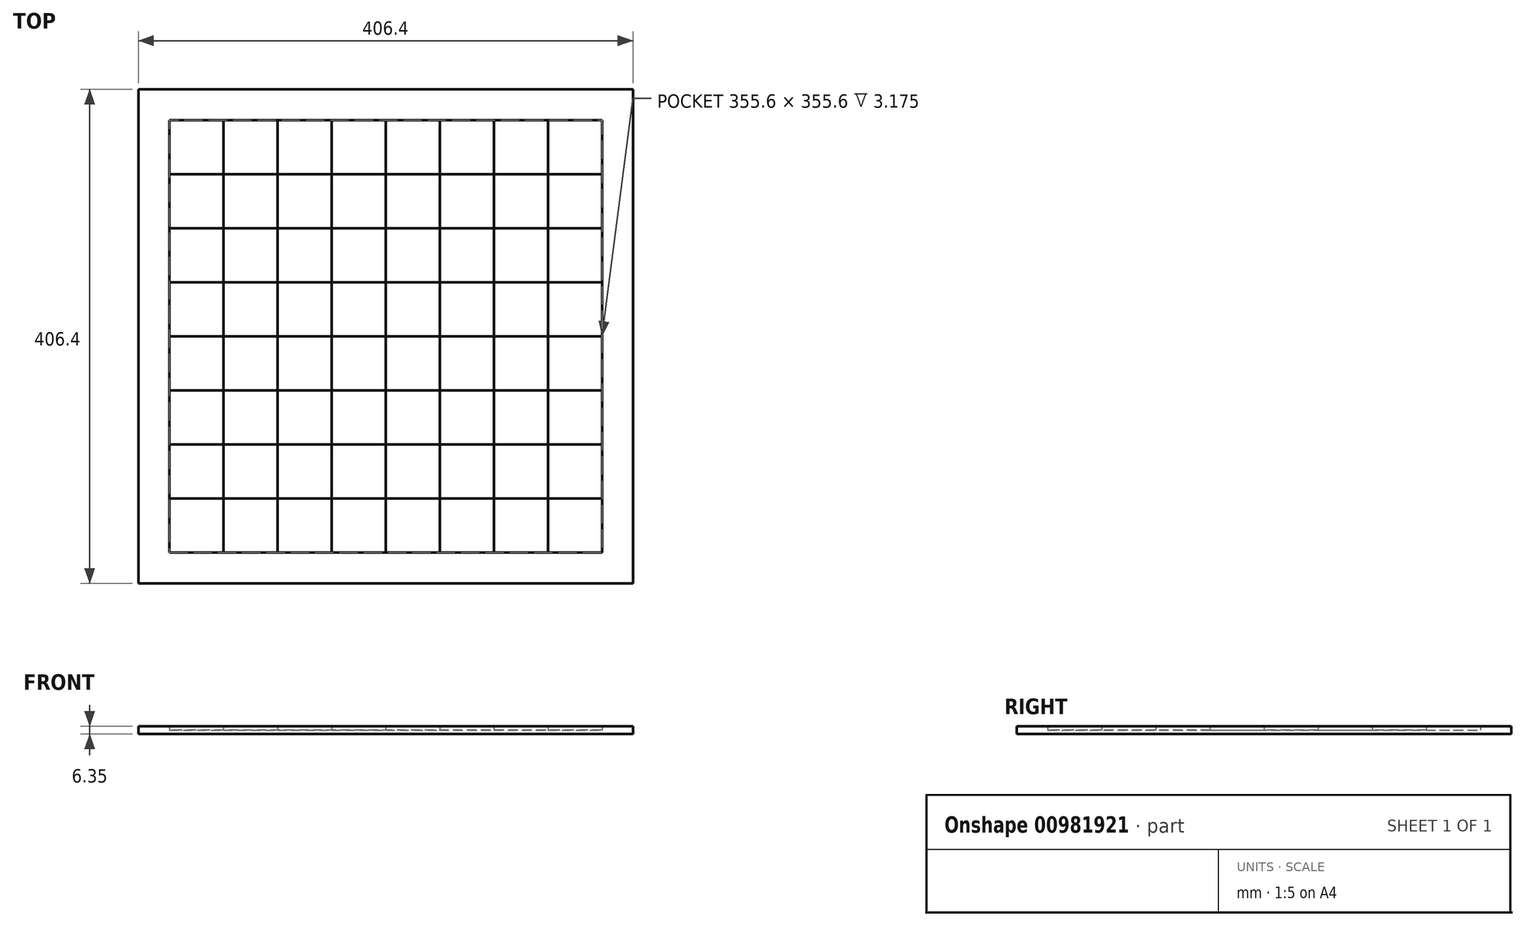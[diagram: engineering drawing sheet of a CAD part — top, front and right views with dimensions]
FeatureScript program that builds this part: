
annotation { "Feature Type Name" : "Feature", "Feature Type Description" : "" }
export const myFeature = defineFeature(function(context is Context, id is Id, definition is map)
    precondition{}
    {
        {
            var Q0;
            Q0=qCreatedBy(makeId("Top.planeOp"),FACE);
            var sketch = newSketch(context, id + "F0", { "sketchPlane" : qUnion([Q0])});
            skLineSegment(sketch, "E0.bottom", {"start": v(203.2, 203.2) * mm, "end": v(-203.2, 203.2) * mm});
            skLineSegment(sketch, "E0.top", {"start": v(203.2, -203.2) * mm, "end": v(-203.2, -203.2) * mm});
            skLineSegment(sketch, "E0.left", {"start": v(203.2, 203.2) * mm, "end": v(203.2, -203.2) * mm});
            skLineSegment(sketch, "E0.right", {"start": v(-203.2, 203.2) * mm, "end": v(-203.2, -203.2) * mm});
            skPoint(sketch, "E0.middle", {"position": v(0, 0) * mm});
            skSolve(sketch);
        }
        {
            var Q0;
            Q0 = qSketchRegion(id + "F0", true);
            extrude(context, id + "F1", {"entities" : qUnion([Q0]), "depth" : 3.17 * mm, "offsetDistance" : 25.4 * mm});
        }
        {
            var Q0;
            Q0=makeQuery(id+"F1.opExtrude","CAP_FACE",FACE,{"disambiguationData":[OSD([sQuery(id+"F0.wireOp",EDGE,"E0.bottom"),sQuery(id+"F0.wireOp",EDGE,"E0.top"),sQuery(id+"F0.wireOp",EDGE,"E0.left"),sQuery(id+"F0.wireOp",EDGE,"E0.right")])],"isStart":false});
            var sketch = newSketch(context, id + "F2", { "sketchPlane" : qUnion([Q0])});
            skLineSegment(sketch, "E1.bottom", {"start": v(203.2, -203.2) * mm, "end": v(-203.2, -203.2) * mm});
            skLineSegment(sketch, "E1.top", {"start": v(203.2, 203.2) * mm, "end": v(-203.2, 203.2) * mm});
            skLineSegment(sketch, "E1.left", {"start": v(203.2, -203.2) * mm, "end": v(203.2, 203.2) * mm});
            skLineSegment(sketch, "E1.right", {"start": v(-203.2, -203.2) * mm, "end": v(-203.2, 203.2) * mm});
            skPoint(sketch, "E1.middle", {"position": v(0, 0) * mm});
            skLineSegment(sketch, "E2.bottom", {"start": v(177.8, -177.8) * mm, "end": v(-177.8, -177.8) * mm});
            skLineSegment(sketch, "E2.top", {"start": v(177.8, 177.8) * mm, "end": v(-177.8, 177.8) * mm});
            skLineSegment(sketch, "E2.left", {"start": v(177.8, -177.8) * mm, "end": v(177.8, 177.8) * mm});
            skLineSegment(sketch, "E2.right", {"start": v(-177.8, -177.8) * mm, "end": v(-177.8, 177.8) * mm});
            skSolve(sketch);
        }
        {
            var Q0;
            Q0 = qSketchRegion(id + "F2", true);
            extrude(context, id + "F3", {"entities" : qUnion([Q0]), "operationType" : NewBodyOperationType.ADD, "depth" : 3.17 * mm, "offsetDistance" : 25.4 * mm});
        }
        {
            var Q0;
            Q0=makeQuery(id+"F1.opExtrude","CAP_FACE",FACE,{"disambiguationData":[OSD([sQuery(id+"F0.wireOp",EDGE,"E0.bottom"),sQuery(id+"F0.wireOp",EDGE,"E0.top"),sQuery(id+"F0.wireOp",EDGE,"E0.left"),sQuery(id+"F0.wireOp",EDGE,"E0.right")])],"isStart":false});
            var sketch = newSketch(context, id + "F4", { "sketchPlane" : qUnion([Q0])});
            skLineSegment(sketch, "E3.bottom", {"start": v(-177.8, 177.8) * mm, "end": v(-133.35, 177.8) * mm});
            skLineSegment(sketch, "E3.top", {"start": v(-177.8, 133.35) * mm, "end": v(-133.35, 133.35) * mm});
            skLineSegment(sketch, "E3.left", {"start": v(-177.8, 177.8) * mm, "end": v(-177.8, 133.35) * mm});
            skLineSegment(sketch, "E3.right", {"start": v(-133.35, 177.8) * mm, "end": v(-133.35, 133.35) * mm});
            skLineSegment(sketch, "E4.1.0.0", {"start": v(-44.45, 177.8) * mm, "end": v(-44.45, 133.35) * mm});
            skLineSegment(sketch, "E4.1.0.1", {"start": v(-88.9, 133.35) * mm, "end": v(-44.45, 133.35) * mm});
            skLineSegment(sketch, "E4.1.0.2", {"start": v(-88.9, 177.8) * mm, "end": v(-88.9, 133.35) * mm});
            skLineSegment(sketch, "E4.1.0.3", {"start": v(-88.9, 177.8) * mm, "end": v(-44.45, 177.8) * mm});
            skLineSegment(sketch, "E4.2.0.0", {"start": v(44.45, 177.8) * mm, "end": v(44.45, 133.35) * mm});
            skLineSegment(sketch, "E4.2.0.1", {"start": v(0, 133.35) * mm, "end": v(44.45, 133.35) * mm});
            skLineSegment(sketch, "E4.2.0.2", {"start": v(0, 177.8) * mm, "end": v(0, 133.35) * mm});
            skLineSegment(sketch, "E4.2.0.3", {"start": v(0, 177.8) * mm, "end": v(44.45, 177.8) * mm});
            skLineSegment(sketch, "E4.3.0.0", {"start": v(133.35, 177.8) * mm, "end": v(133.35, 133.35) * mm});
            skLineSegment(sketch, "E4.3.0.1", {"start": v(88.9, 133.35) * mm, "end": v(133.35, 133.35) * mm});
            skLineSegment(sketch, "E4.3.0.2", {"start": v(88.9, 177.8) * mm, "end": v(88.9, 133.35) * mm});
            skLineSegment(sketch, "E4.3.0.3", {"start": v(88.9, 177.8) * mm, "end": v(133.35, 177.8) * mm});
            skLineSegment(sketch, "E4.direction1", {"start": v(-177.8, 133.35) * mm, "end": v(-88.9, 133.35) * mm, "construction": true});
            skLineSegment(sketch, "E5.bottom", {"start": v(-133.35, 133.35) * mm, "end": v(-88.9, 133.35) * mm});
            skLineSegment(sketch, "E5.top", {"start": v(-133.35, 88.9) * mm, "end": v(-88.9, 88.9) * mm});
            skLineSegment(sketch, "E5.left", {"start": v(-133.35, 133.35) * mm, "end": v(-133.35, 88.9) * mm});
            skLineSegment(sketch, "E5.right", {"start": v(-88.9, 133.35) * mm, "end": v(-88.9, 88.9) * mm});
            skLineSegment(sketch, "E6.1.0.0", {"start": v(-44.45, 133.35) * mm, "end": v(-44.45, 88.9) * mm});
            skLineSegment(sketch, "E6.1.0.1", {"start": v(-44.45, 88.9) * mm, "end": v(0, 88.9) * mm});
            skLineSegment(sketch, "E6.1.0.2", {"start": v(0, 133.35) * mm, "end": v(0, 88.9) * mm});
            skLineSegment(sketch, "E6.1.0.3", {"start": v(-44.45, 133.35) * mm, "end": v(0, 133.35) * mm});
            skLineSegment(sketch, "E6.2.0.0", {"start": v(44.45, 133.35) * mm, "end": v(44.45, 88.9) * mm});
            skLineSegment(sketch, "E6.2.0.1", {"start": v(44.45, 88.9) * mm, "end": v(88.9, 88.9) * mm});
            skLineSegment(sketch, "E6.2.0.2", {"start": v(88.9, 133.35) * mm, "end": v(88.9, 88.9) * mm});
            skLineSegment(sketch, "E6.2.0.3", {"start": v(44.45, 133.35) * mm, "end": v(88.9, 133.35) * mm});
            skLineSegment(sketch, "E6.3.0.0", {"start": v(133.35, 133.35) * mm, "end": v(133.35, 88.9) * mm});
            skLineSegment(sketch, "E6.3.0.1", {"start": v(133.35, 88.9) * mm, "end": v(177.8, 88.9) * mm});
            skLineSegment(sketch, "E6.3.0.2", {"start": v(177.8, 133.35) * mm, "end": v(177.8, 88.9) * mm});
            skLineSegment(sketch, "E6.3.0.3", {"start": v(133.35, 133.35) * mm, "end": v(177.8, 133.35) * mm});
            skLineSegment(sketch, "E6.direction1", {"start": v(-133.35, 88.9) * mm, "end": v(-44.45, 88.9) * mm, "construction": true});
            skLineSegment(sketch, "E7.0.1.0", {"start": v(-44.45, 44.45) * mm, "end": v(-44.45, 0) * mm});
            skLineSegment(sketch, "E7.0.1.1", {"start": v(-133.35, 44.45) * mm, "end": v(-133.35, 0) * mm});
            skLineSegment(sketch, "E7.0.1.2", {"start": v(-88.9, 88.9) * mm, "end": v(-88.9, 44.45) * mm});
            skLineSegment(sketch, "E7.0.1.3", {"start": v(-44.45, 88.9) * mm, "end": v(-44.45, 44.45) * mm});
            skLineSegment(sketch, "E7.0.1.4", {"start": v(88.9, 88.9) * mm, "end": v(88.9, 44.45) * mm});
            skLineSegment(sketch, "E7.0.1.5", {"start": v(133.35, 0) * mm, "end": v(177.8, 0) * mm});
            skLineSegment(sketch, "E7.0.1.6", {"start": v(44.45, 88.9) * mm, "end": v(44.45, 44.45) * mm});
            skLineSegment(sketch, "E7.0.1.7", {"start": v(-88.9, 44.45) * mm, "end": v(-44.45, 44.45) * mm});
            skLineSegment(sketch, "E7.0.1.8", {"start": v(44.45, 0) * mm, "end": v(88.9, 0) * mm});
            skLineSegment(sketch, "E7.0.1.9", {"start": v(133.35, 44.45) * mm, "end": v(177.8, 44.45) * mm});
            skLineSegment(sketch, "E7.0.1.10", {"start": v(0, 44.45) * mm, "end": v(0, 0) * mm});
            skLineSegment(sketch, "E7.0.1.11", {"start": v(-88.9, 44.45) * mm, "end": v(-88.9, 0) * mm});
            skLineSegment(sketch, "E7.0.1.12", {"start": v(44.45, 44.45) * mm, "end": v(44.45, 0) * mm});
            skLineSegment(sketch, "E7.0.1.13", {"start": v(-44.45, 44.45) * mm, "end": v(0, 44.45) * mm});
            skLineSegment(sketch, "E7.0.1.14", {"start": v(-177.8, 88.9) * mm, "end": v(-133.35, 88.9) * mm});
            skLineSegment(sketch, "E7.0.1.15", {"start": v(0, 44.45) * mm, "end": v(44.45, 44.45) * mm});
            skLineSegment(sketch, "E7.0.1.16", {"start": v(177.8, 44.45) * mm, "end": v(177.8, 0) * mm});
            skLineSegment(sketch, "E7.0.1.17", {"start": v(88.9, 44.45) * mm, "end": v(88.9, 0) * mm});
            skLineSegment(sketch, "E7.0.1.18", {"start": v(133.35, 88.9) * mm, "end": v(133.35, 44.45) * mm});
            skLineSegment(sketch, "E7.0.1.19", {"start": v(88.9, 88.9) * mm, "end": v(133.35, 88.9) * mm});
            skLineSegment(sketch, "E7.0.1.20", {"start": v(-133.35, 0) * mm, "end": v(-88.9, 0) * mm});
            skLineSegment(sketch, "E7.0.1.21", {"start": v(-44.45, 0) * mm, "end": v(0, 0) * mm});
            skLineSegment(sketch, "E7.0.1.22", {"start": v(-177.8, 44.45) * mm, "end": v(-133.35, 44.45) * mm});
            skLineSegment(sketch, "E7.0.1.23", {"start": v(0, 88.9) * mm, "end": v(0, 44.45) * mm});
            skLineSegment(sketch, "E7.0.1.24", {"start": v(44.45, 44.45) * mm, "end": v(88.9, 44.45) * mm});
            skLineSegment(sketch, "E7.0.1.25", {"start": v(133.35, 44.45) * mm, "end": v(133.35, 0) * mm});
            skLineSegment(sketch, "E7.0.1.26", {"start": v(88.9, 44.45) * mm, "end": v(133.35, 44.45) * mm});
            skLineSegment(sketch, "E7.0.1.27", {"start": v(-88.9, 88.9) * mm, "end": v(-44.45, 88.9) * mm});
            skLineSegment(sketch, "E7.0.1.28", {"start": v(-177.8, 88.9) * mm, "end": v(-177.8, 44.45) * mm});
            skLineSegment(sketch, "E7.0.1.29", {"start": v(-133.35, 88.9) * mm, "end": v(-133.35, 44.45) * mm});
            skLineSegment(sketch, "E7.0.1.30", {"start": v(-133.35, 44.45) * mm, "end": v(-88.9, 44.45) * mm});
            skLineSegment(sketch, "E7.0.1.31", {"start": v(0, 88.9) * mm, "end": v(44.45, 88.9) * mm});
            skLineSegment(sketch, "E7.0.2.0", {"start": v(-44.45, -44.45) * mm, "end": v(-44.45, -88.9) * mm});
            skLineSegment(sketch, "E7.0.2.1", {"start": v(-133.35, -44.45) * mm, "end": v(-133.35, -88.9) * mm});
            skLineSegment(sketch, "E7.0.2.2", {"start": v(-88.9, 0) * mm, "end": v(-88.9, -44.45) * mm});
            skLineSegment(sketch, "E7.0.2.3", {"start": v(-44.45, 0) * mm, "end": v(-44.45, -44.45) * mm});
            skLineSegment(sketch, "E7.0.2.4", {"start": v(88.9, 0) * mm, "end": v(88.9, -44.45) * mm});
            skLineSegment(sketch, "E7.0.2.5", {"start": v(133.35, -88.9) * mm, "end": v(177.8, -88.9) * mm});
            skLineSegment(sketch, "E7.0.2.6", {"start": v(44.45, 0) * mm, "end": v(44.45, -44.45) * mm});
            skLineSegment(sketch, "E7.0.2.7", {"start": v(-88.9, -44.45) * mm, "end": v(-44.45, -44.45) * mm});
            skLineSegment(sketch, "E7.0.2.8", {"start": v(44.45, -88.9) * mm, "end": v(88.9, -88.9) * mm});
            skLineSegment(sketch, "E7.0.2.9", {"start": v(133.35, -44.45) * mm, "end": v(177.8, -44.45) * mm});
            skLineSegment(sketch, "E7.0.2.10", {"start": v(0, -44.45) * mm, "end": v(0, -88.9) * mm});
            skLineSegment(sketch, "E7.0.2.11", {"start": v(-88.9, -44.45) * mm, "end": v(-88.9, -88.9) * mm});
            skLineSegment(sketch, "E7.0.2.12", {"start": v(44.45, -44.45) * mm, "end": v(44.45, -88.9) * mm});
            skLineSegment(sketch, "E7.0.2.13", {"start": v(-44.45, -44.45) * mm, "end": v(0, -44.45) * mm});
            skLineSegment(sketch, "E7.0.2.14", {"start": v(-177.8, 0) * mm, "end": v(-133.35, 0) * mm});
            skLineSegment(sketch, "E7.0.2.15", {"start": v(0, -44.45) * mm, "end": v(44.45, -44.45) * mm});
            skLineSegment(sketch, "E7.0.2.16", {"start": v(177.8, -44.45) * mm, "end": v(177.8, -88.9) * mm});
            skLineSegment(sketch, "E7.0.2.17", {"start": v(88.9, -44.45) * mm, "end": v(88.9, -88.9) * mm});
            skLineSegment(sketch, "E7.0.2.18", {"start": v(133.35, 0) * mm, "end": v(133.35, -44.45) * mm});
            skLineSegment(sketch, "E7.0.2.19", {"start": v(88.9, 0) * mm, "end": v(133.35, 0) * mm});
            skLineSegment(sketch, "E7.0.2.20", {"start": v(-133.35, -88.9) * mm, "end": v(-88.9, -88.9) * mm});
            skLineSegment(sketch, "E7.0.2.21", {"start": v(-44.45, -88.9) * mm, "end": v(0, -88.9) * mm});
            skLineSegment(sketch, "E7.0.2.22", {"start": v(-177.8, -44.45) * mm, "end": v(-133.35, -44.45) * mm});
            skLineSegment(sketch, "E7.0.2.23", {"start": v(0, 0) * mm, "end": v(0, -44.45) * mm});
            skLineSegment(sketch, "E7.0.2.24", {"start": v(44.45, -44.45) * mm, "end": v(88.9, -44.45) * mm});
            skLineSegment(sketch, "E7.0.2.25", {"start": v(133.35, -44.45) * mm, "end": v(133.35, -88.9) * mm});
            skLineSegment(sketch, "E7.0.2.26", {"start": v(88.9, -44.45) * mm, "end": v(133.35, -44.45) * mm});
            skLineSegment(sketch, "E7.0.2.27", {"start": v(-88.9, 0) * mm, "end": v(-44.45, 0) * mm});
            skLineSegment(sketch, "E7.0.2.28", {"start": v(-177.8, 0) * mm, "end": v(-177.8, -44.45) * mm});
            skLineSegment(sketch, "E7.0.2.29", {"start": v(-133.35, 0) * mm, "end": v(-133.35, -44.45) * mm});
            skLineSegment(sketch, "E7.0.2.30", {"start": v(-133.35, -44.45) * mm, "end": v(-88.9, -44.45) * mm});
            skLineSegment(sketch, "E7.0.2.31", {"start": v(0, 0) * mm, "end": v(44.45, 0) * mm});
            skLineSegment(sketch, "E7.0.3.0", {"start": v(-44.45, -133.35) * mm, "end": v(-44.45, -177.8) * mm});
            skLineSegment(sketch, "E7.0.3.1", {"start": v(-133.35, -133.35) * mm, "end": v(-133.35, -177.8) * mm});
            skLineSegment(sketch, "E7.0.3.2", {"start": v(-88.9, -88.9) * mm, "end": v(-88.9, -133.35) * mm});
            skLineSegment(sketch, "E7.0.3.3", {"start": v(-44.45, -88.9) * mm, "end": v(-44.45, -133.35) * mm});
            skLineSegment(sketch, "E7.0.3.4", {"start": v(88.9, -88.9) * mm, "end": v(88.9, -133.35) * mm});
            skLineSegment(sketch, "E7.0.3.5", {"start": v(133.35, -177.8) * mm, "end": v(177.8, -177.8) * mm});
            skLineSegment(sketch, "E7.0.3.6", {"start": v(44.45, -88.9) * mm, "end": v(44.45, -133.35) * mm});
            skLineSegment(sketch, "E7.0.3.7", {"start": v(-88.9, -133.35) * mm, "end": v(-44.45, -133.35) * mm});
            skLineSegment(sketch, "E7.0.3.8", {"start": v(44.45, -177.8) * mm, "end": v(88.9, -177.8) * mm});
            skLineSegment(sketch, "E7.0.3.9", {"start": v(133.35, -133.35) * mm, "end": v(177.8, -133.35) * mm});
            skLineSegment(sketch, "E7.0.3.10", {"start": v(0, -133.35) * mm, "end": v(0, -177.8) * mm});
            skLineSegment(sketch, "E7.0.3.11", {"start": v(-88.9, -133.35) * mm, "end": v(-88.9, -177.8) * mm});
            skLineSegment(sketch, "E7.0.3.12", {"start": v(44.45, -133.35) * mm, "end": v(44.45, -177.8) * mm});
            skLineSegment(sketch, "E7.0.3.13", {"start": v(-44.45, -133.35) * mm, "end": v(0, -133.35) * mm});
            skLineSegment(sketch, "E7.0.3.14", {"start": v(-177.8, -88.9) * mm, "end": v(-133.35, -88.9) * mm});
            skLineSegment(sketch, "E7.0.3.15", {"start": v(0, -133.35) * mm, "end": v(44.45, -133.35) * mm});
            skLineSegment(sketch, "E7.0.3.16", {"start": v(177.8, -133.35) * mm, "end": v(177.8, -177.8) * mm});
            skLineSegment(sketch, "E7.0.3.17", {"start": v(88.9, -133.35) * mm, "end": v(88.9, -177.8) * mm});
            skLineSegment(sketch, "E7.0.3.18", {"start": v(133.35, -88.9) * mm, "end": v(133.35, -133.35) * mm});
            skLineSegment(sketch, "E7.0.3.19", {"start": v(88.9, -88.9) * mm, "end": v(133.35, -88.9) * mm});
            skLineSegment(sketch, "E7.0.3.20", {"start": v(-133.35, -177.8) * mm, "end": v(-88.9, -177.8) * mm});
            skLineSegment(sketch, "E7.0.3.21", {"start": v(-44.45, -177.8) * mm, "end": v(0, -177.8) * mm});
            skLineSegment(sketch, "E7.0.3.22", {"start": v(-177.8, -133.35) * mm, "end": v(-133.35, -133.35) * mm});
            skLineSegment(sketch, "E7.0.3.23", {"start": v(0, -88.9) * mm, "end": v(0, -133.35) * mm});
            skLineSegment(sketch, "E7.0.3.24", {"start": v(44.45, -133.35) * mm, "end": v(88.9, -133.35) * mm});
            skLineSegment(sketch, "E7.0.3.25", {"start": v(133.35, -133.35) * mm, "end": v(133.35, -177.8) * mm});
            skLineSegment(sketch, "E7.0.3.26", {"start": v(88.9, -133.35) * mm, "end": v(133.35, -133.35) * mm});
            skLineSegment(sketch, "E7.0.3.27", {"start": v(-88.9, -88.9) * mm, "end": v(-44.45, -88.9) * mm});
            skLineSegment(sketch, "E7.0.3.28", {"start": v(-177.8, -88.9) * mm, "end": v(-177.8, -133.35) * mm});
            skLineSegment(sketch, "E7.0.3.29", {"start": v(-133.35, -88.9) * mm, "end": v(-133.35, -133.35) * mm});
            skLineSegment(sketch, "E7.0.3.30", {"start": v(-133.35, -133.35) * mm, "end": v(-88.9, -133.35) * mm});
            skLineSegment(sketch, "E7.0.3.31", {"start": v(0, -88.9) * mm, "end": v(44.45, -88.9) * mm});
            skLineSegment(sketch, "E7.direction1", {"start": v(-177.8, 133.35) * mm, "end": v(-152.4, 133.35) * mm, "construction": true});
            skLineSegment(sketch, "E7.direction2", {"start": v(-177.8, 133.35) * mm, "end": v(-177.8, 44.45) * mm, "construction": true});
            skSolve(sketch);
        }
        {
            var Q0;
            Q0=makeQuery(id+"F4.imprint","IMPRINT",FACE,{"disambiguationData":[TD([[makeQuery(id+"F4.imprint","IMPRINT",EDGE,{"derivedFrom":sQuery(id+"F4.wireOp",EDGE,"E3.bottom")}),1.0]])]});
            var Q1;
            Q1=makeQuery(id+"F4.imprint","IMPRINT",FACE,{"disambiguationData":[TD([[makeQuery(id+"F4.imprint","IMPRINT",EDGE,{"derivedFrom":sQuery(id+"F4.wireOp",EDGE,"E4.1.0.0")}),-1.0]])]});
            var Q2;
            Q2=makeQuery(id+"F4.imprint","IMPRINT",FACE,{"disambiguationData":[TD([[makeQuery(id+"F4.imprint","IMPRINT",EDGE,{"derivedFrom":sQuery(id+"F4.wireOp",EDGE,"E4.2.0.0")}),-1.0]])]});
            var Q3;
            Q3=makeQuery(id+"F4.imprint","IMPRINT",FACE,{"disambiguationData":[TD([[makeQuery(id+"F4.imprint","IMPRINT",EDGE,{"derivedFrom":sQuery(id+"F4.wireOp",EDGE,"E4.3.0.0")}),-1.0]])]});
            var Q4;
            Q4=makeQuery(id+"F4.imprint","IMPRINT",FACE,{"disambiguationData":[TD([[makeQuery(id+"F4.imprint","IMPRINT",EDGE,{"derivedFrom":sQuery(id+"F4.wireOp",EDGE,"E5.bottom")}),-1.0]])]});
            var Q5;
            Q5=makeQuery(id+"F4.imprint","IMPRINT",FACE,{"disambiguationData":[TD([[makeQuery(id+"F4.imprint","IMPRINT",EDGE,{"derivedFrom":sQuery(id+"F4.wireOp",EDGE,"E6.1.0.0")}),1.0]])]});
            var Q6;
            Q6=makeQuery(id+"F4.imprint","IMPRINT",FACE,{"disambiguationData":[TD([[makeQuery(id+"F4.imprint","IMPRINT",EDGE,{"derivedFrom":sQuery(id+"F4.wireOp",EDGE,"E6.2.0.0")}),1.0]])]});
            var Q7;
            Q7=makeQuery(id+"F4.imprint","IMPRINT",FACE,{"disambiguationData":[TD([[makeQuery(id+"F4.imprint","IMPRINT",EDGE,{"derivedFrom":sQuery(id+"F4.wireOp",EDGE,"E6.3.0.0")}),1.0]])]});
            var Q8;
            Q8=makeQuery(id+"F4.imprint","IMPRINT",FACE,{"disambiguationData":[TD([[makeQuery(id+"F4.imprint","IMPRINT",EDGE,{"derivedFrom":sQuery(id+"F4.wireOp",EDGE,"E7.0.1.4")}),1.0]])]});
            var Q9;
            Q9=makeQuery(id+"F4.imprint","IMPRINT",FACE,{"disambiguationData":[TD([[makeQuery(id+"F4.imprint","IMPRINT",EDGE,{"derivedFrom":sQuery(id+"F4.wireOp",EDGE,"E7.0.1.6")}),-1.0]])]});
            var Q10;
            Q10=makeQuery(id+"F4.imprint","IMPRINT",FACE,{"disambiguationData":[TD([[makeQuery(id+"F4.imprint","IMPRINT",EDGE,{"derivedFrom":sQuery(id+"F4.wireOp",EDGE,"E7.0.1.2")}),1.0]])]});
            var Q11;
            Q11=makeQuery(id+"F4.imprint","IMPRINT",FACE,{"disambiguationData":[TD([[makeQuery(id+"F4.imprint","IMPRINT",EDGE,{"derivedFrom":sQuery(id+"F4.wireOp",EDGE,"E7.0.1.14")}),-1.0]])]});
            var Q12;
            Q12=makeQuery(id+"F4.imprint","IMPRINT",FACE,{"disambiguationData":[TD([[makeQuery(id+"F4.imprint","IMPRINT",EDGE,{"derivedFrom":sQuery(id+"F4.wireOp",EDGE,"E7.0.1.1")}),1.0]])]});
            var Q13;
            Q13=makeQuery(id+"F4.imprint","IMPRINT",FACE,{"disambiguationData":[TD([[makeQuery(id+"F4.imprint","IMPRINT",EDGE,{"derivedFrom":sQuery(id+"F4.wireOp",EDGE,"E7.0.1.0")}),1.0]])]});
            var Q14;
            Q14=makeQuery(id+"F4.imprint","IMPRINT",FACE,{"disambiguationData":[TD([[makeQuery(id+"F4.imprint","IMPRINT",EDGE,{"derivedFrom":sQuery(id+"F4.wireOp",EDGE,"E7.0.1.8")}),1.0]])]});
            var Q15;
            Q15=makeQuery(id+"F4.imprint","IMPRINT",FACE,{"disambiguationData":[TD([[makeQuery(id+"F4.imprint","IMPRINT",EDGE,{"derivedFrom":sQuery(id+"F4.wireOp",EDGE,"E7.0.1.5")}),1.0]])]});
            var Q16;
            Q16=makeQuery(id+"F4.imprint","IMPRINT",FACE,{"disambiguationData":[TD([[makeQuery(id+"F4.imprint","IMPRINT",EDGE,{"derivedFrom":sQuery(id+"F4.wireOp",EDGE,"E7.0.2.4")}),1.0]])]});
            var Q17;
            Q17=makeQuery(id+"F4.imprint","IMPRINT",FACE,{"disambiguationData":[TD([[makeQuery(id+"F4.imprint","IMPRINT",EDGE,{"derivedFrom":sQuery(id+"F4.wireOp",EDGE,"E7.0.2.6")}),-1.0]])]});
            var Q18;
            Q18=makeQuery(id+"F4.imprint","IMPRINT",FACE,{"disambiguationData":[TD([[makeQuery(id+"F4.imprint","IMPRINT",EDGE,{"derivedFrom":sQuery(id+"F4.wireOp",EDGE,"E7.0.2.2")}),1.0]])]});
            var Q19;
            Q19=makeQuery(id+"F4.imprint","IMPRINT",FACE,{"disambiguationData":[TD([[makeQuery(id+"F4.imprint","IMPRINT",EDGE,{"derivedFrom":sQuery(id+"F4.wireOp",EDGE,"E7.0.2.14")}),-1.0]])]});
            var Q20;
            Q20=makeQuery(id+"F4.imprint","IMPRINT",FACE,{"disambiguationData":[TD([[makeQuery(id+"F4.imprint","IMPRINT",EDGE,{"derivedFrom":sQuery(id+"F4.wireOp",EDGE,"E7.0.2.1")}),1.0]])]});
            var Q21;
            Q21=makeQuery(id+"F4.imprint","IMPRINT",FACE,{"disambiguationData":[TD([[makeQuery(id+"F4.imprint","IMPRINT",EDGE,{"derivedFrom":sQuery(id+"F4.wireOp",EDGE,"E7.0.2.0")}),1.0]])]});
            var Q22;
            Q22=makeQuery(id+"F4.imprint","IMPRINT",FACE,{"disambiguationData":[TD([[makeQuery(id+"F4.imprint","IMPRINT",EDGE,{"derivedFrom":sQuery(id+"F4.wireOp",EDGE,"E7.0.2.8")}),1.0]])]});
            var Q23;
            Q23=makeQuery(id+"F4.imprint","IMPRINT",FACE,{"disambiguationData":[TD([[makeQuery(id+"F4.imprint","IMPRINT",EDGE,{"derivedFrom":sQuery(id+"F4.wireOp",EDGE,"E7.0.2.5")}),1.0]])]});
            var Q24;
            Q24=makeQuery(id+"F4.imprint","IMPRINT",FACE,{"disambiguationData":[TD([[makeQuery(id+"F4.imprint","IMPRINT",EDGE,{"derivedFrom":sQuery(id+"F4.wireOp",EDGE,"E7.0.3.4")}),1.0]])]});
            var Q25;
            Q25=makeQuery(id+"F4.imprint","IMPRINT",FACE,{"disambiguationData":[TD([[makeQuery(id+"F4.imprint","IMPRINT",EDGE,{"derivedFrom":sQuery(id+"F4.wireOp",EDGE,"E7.0.3.6")}),-1.0]])]});
            var Q26;
            Q26=makeQuery(id+"F4.imprint","IMPRINT",FACE,{"disambiguationData":[TD([[makeQuery(id+"F4.imprint","IMPRINT",EDGE,{"derivedFrom":sQuery(id+"F4.wireOp",EDGE,"E7.0.3.2")}),1.0]])]});
            var Q27;
            Q27=makeQuery(id+"F4.imprint","IMPRINT",FACE,{"disambiguationData":[TD([[makeQuery(id+"F4.imprint","IMPRINT",EDGE,{"derivedFrom":sQuery(id+"F4.wireOp",EDGE,"E7.0.3.14")}),-1.0]])]});
            var Q28;
            Q28=makeQuery(id+"F4.imprint","IMPRINT",FACE,{"disambiguationData":[TD([[makeQuery(id+"F4.imprint","IMPRINT",EDGE,{"derivedFrom":sQuery(id+"F4.wireOp",EDGE,"E7.0.3.1")}),1.0]])]});
            var Q29;
            Q29=makeQuery(id+"F4.imprint","IMPRINT",FACE,{"disambiguationData":[TD([[makeQuery(id+"F4.imprint","IMPRINT",EDGE,{"derivedFrom":sQuery(id+"F4.wireOp",EDGE,"E7.0.3.0")}),1.0]])]});
            var Q30;
            Q30=makeQuery(id+"F4.imprint","IMPRINT",FACE,{"disambiguationData":[TD([[makeQuery(id+"F4.imprint","IMPRINT",EDGE,{"derivedFrom":sQuery(id+"F4.wireOp",EDGE,"E7.0.3.8")}),-1.0]])]});
            var Q31;
            Q31=makeQuery(id+"F4.imprint","IMPRINT",FACE,{"disambiguationData":[TD([[makeQuery(id+"F4.imprint","IMPRINT",EDGE,{"derivedFrom":sQuery(id+"F4.wireOp",EDGE,"E7.0.3.5")}),-1.0]])]});
            extrude(context, id + "F5", {"entities" : qUnion([Q0, Q1, Q2, Q3, Q4, Q5, Q6, Q7, Q8, Q9, Q10, Q11, Q12, Q13, Q14, Q15, Q16, Q17, Q18, Q19, Q20, Q21, Q22, Q23, Q24, Q25, Q26, Q27, Q28, Q29, Q30, Q31]), "depth" : 3.17 * mm, "offsetDistance" : 25.4 * mm});
        }
    });
